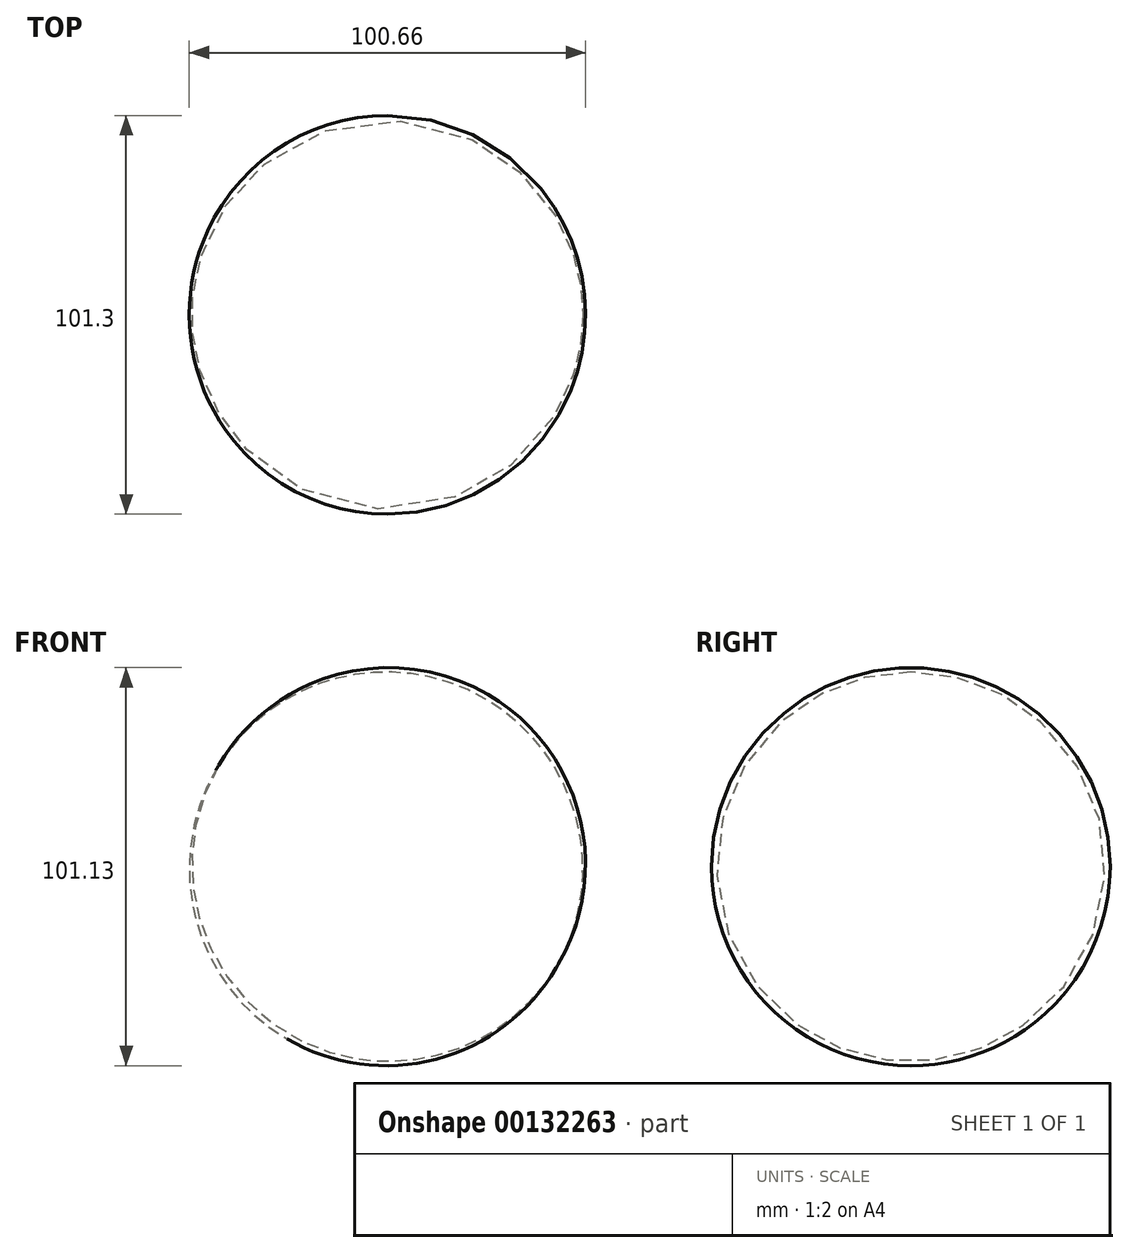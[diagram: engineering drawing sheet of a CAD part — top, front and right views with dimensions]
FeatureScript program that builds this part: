
annotation { "Feature Type Name" : "Feature", "Feature Type Description" : "" }
export const myFeature = defineFeature(function(context is Context, id is Id, definition is map)
    precondition{}
    {
        {
            var Q0;
            Q0=qCreatedBy(makeId("Front.planeOp"),FACE);
            var sketch = newSketch(context, id + "F0", { "sketchPlane" : qUnion([Q0])});
            skCircle(sketch, "E0", {"center": v(-25.56, 13.5) * mm, "radius": 50 * mm});
            skLineSegment(sketch, "E1", {"start": v(17.96, -11.12) * mm, "end": v(-68.42, 39.25) * mm});
            skSolve(sketch);
        }
        {
            var Q0;
            {var subQ0=sQuery(id+"F0.wireOp",EDGE,"E1");Q0=makeQuery(id+"F0.imprint","IMPRINT",FACE,{"disambiguationData":[TD([[makeQuery(id+"F0.imprint","IMPRINT",EDGE,{"derivedFrom":subQ0}),1.0]])]});}
            var Q1;
            Q1=sQuery(id+"F0.wireOp",EDGE,"E1");
            revolve(context, id + "F1", {"entities" : qUnion([Q0]), "axis" : qUnion([Q1]), "revolveType" : RevolveType.FULL});
        }
    });
